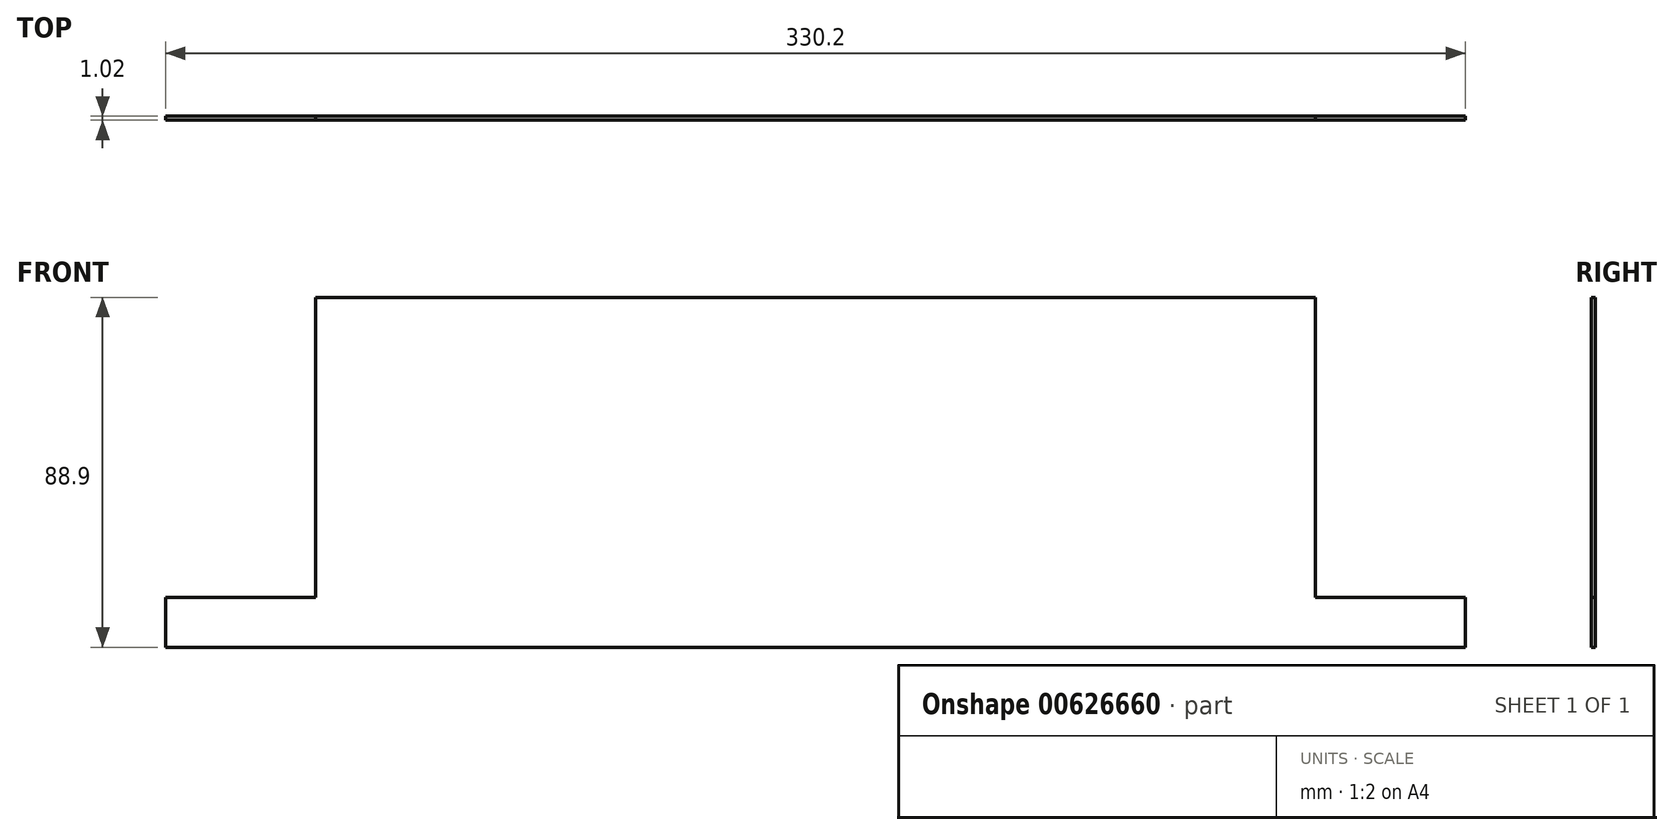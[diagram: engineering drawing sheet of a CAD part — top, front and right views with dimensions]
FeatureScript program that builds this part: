
annotation { "Feature Type Name" : "Feature", "Feature Type Description" : "" }
export const myFeature = defineFeature(function(context is Context, id is Id, definition is map)
    precondition{}
    {
        {
            var Q0;
            Q0=qCreatedBy(makeId("Front.planeOp"),FACE);
            var sketch = newSketch(context, id + "F0", { "sketchPlane" : qUnion([Q0])});
            skLineSegment(sketch, "E0.bottom", {"start": v(0, 0) * mm, "end": v(330.2, 0) * mm});
            skLineSegment(sketch, "E0.top", {"start": v(0, 88.9) * mm, "end": v(330.2, 88.9) * mm});
            skLineSegment(sketch, "E0.left", {"start": v(0, 0) * mm, "end": v(0, 88.9) * mm});
            skLineSegment(sketch, "E0.right", {"start": v(330.2, 0) * mm, "end": v(330.2, 88.9) * mm});
            skSolve(sketch);
        }
        {
            var Q0;
            Q0=makeQuery(id+"F0.imprint","IMPRINT",FACE,{"disambiguationData":[TD([[makeQuery(id+"F0.imprint","IMPRINT",EDGE,{"derivedFrom":sQuery(id+"F0.wireOp",EDGE,"E0.bottom")}),1.0]])]});
            extrude(context, id + "F1", {"entities" : qUnion([Q0]), "depth" : 1.02 * mm, "offsetDistance" : 25.4 * mm});
        }
        {
            var Q0;
            Q0=makeQuery(id+"F1.opExtrude","CAP_FACE",FACE,{"disambiguationData":[OSD([sQuery(id+"F0.wireOp",EDGE,"E0.bottom"),sQuery(id+"F0.wireOp",EDGE,"E0.top"),sQuery(id+"F0.wireOp",EDGE,"E0.left"),sQuery(id+"F0.wireOp",EDGE,"E0.right")])],"isStart":false});
            var sketch = newSketch(context, id + "F2", { "sketchPlane" : qUnion([Q0])});
            skLineSegment(sketch, "E1.bottom", {"start": v(0, 88.9) * mm, "end": v(38.1, 88.9) * mm});
            skLineSegment(sketch, "E1.top", {"start": v(0, 12.7) * mm, "end": v(38.1, 12.7) * mm});
            skLineSegment(sketch, "E1.left", {"start": v(0, 88.9) * mm, "end": v(0, 12.7) * mm});
            skLineSegment(sketch, "E1.right", {"start": v(38.1, 88.9) * mm, "end": v(38.1, 12.7) * mm});
            skSolve(sketch);
        }
        {
            var Q0;
            Q0=makeQuery(id+"F2.imprint","IMPRINT",FACE,{"disambiguationData":[TD([[makeQuery(id+"F2.imprint","IMPRINT",EDGE,{"derivedFrom":sQuery(id+"F2.wireOp",EDGE,"E1.bottom")}),-1.0]])]});
            extrude(context, id + "F3", {"entities" : qUnion([Q0]), "operationType" : NewBodyOperationType.REMOVE, "oppositeDirection" : true, "depth" : 25.4 * mm, "offsetDistance" : 25.4 * mm});
        }
        {
            var Q0;
            Q0=makeQuery(id+"F1.opExtrude","CAP_FACE",FACE,{"disambiguationData":[OSD([sQuery(id+"F0.wireOp",EDGE,"E0.bottom"),sQuery(id+"F0.wireOp",EDGE,"E0.top"),sQuery(id+"F0.wireOp",EDGE,"E0.left"),sQuery(id+"F0.wireOp",EDGE,"E0.right")])],"isStart":false});
            var sketch = newSketch(context, id + "F4", { "sketchPlane" : qUnion([Q0])});
            skLineSegment(sketch, "E2.bottom", {"start": v(330.2, 88.9) * mm, "end": v(292.1, 88.9) * mm});
            skLineSegment(sketch, "E2.top", {"start": v(330.2, 12.7) * mm, "end": v(292.1, 12.7) * mm});
            skLineSegment(sketch, "E2.left", {"start": v(330.2, 88.9) * mm, "end": v(330.2, 12.7) * mm});
            skLineSegment(sketch, "E2.right", {"start": v(292.1, 88.9) * mm, "end": v(292.1, 12.7) * mm});
            skSolve(sketch);
        }
        {
            var Q0;
            Q0=makeQuery(id+"F4.imprint","IMPRINT",FACE,{"disambiguationData":[TD([[makeQuery(id+"F4.imprint","IMPRINT",EDGE,{"derivedFrom":sQuery(id+"F4.wireOp",EDGE,"E2.bottom")}),-1.0]])]});
            extrude(context, id + "F5", {"entities" : qUnion([Q0]), "operationType" : NewBodyOperationType.REMOVE, "oppositeDirection" : true, "depth" : 25.4 * mm, "offsetDistance" : 25.4 * mm});
        }
    });
